# Revit family: XDiverter_Valve_Trim-American_Standard-Studio_S-T105.740
name_source: partatom
category: Plumbing Fixtures
revit_build: Autodesk Revit 2014 (Build: 20130308_1515(x64)
units: mm (PartAtom-declared; Revit-internal decimal feet)

## types (1)
- T105.740
    ADA Compliant = Yes
    Assembly Code = D2020300
    CW Connection = Yes
    CWFU = 3
    Connection Description = 1/2'' NPT Outlet Connection
    Default Elevation = 40"
    Description = Studio S Two-Handle Thermostat
    Distance From Wall = 2"
    Finish = Brass-American Standard-002-Polished Chrome
    HW Connection = Yes
    HWFU = 3
    Height = 3 13/16"
    Installation Type = Wall Mounted
    Length = 7 7/8"
    Manufacturer = American Standard
    Material = Brass-American Standard-002-Polished Chrome
    Model = T105.740
    Outlet Diameter Connection = 0"
    Price = Prices may vary. Please consult Manufacturer Representative for most up-to-date price list.
    Product Documentation Link = https://www.americanstandard-us.com
    Product Page URL = https://www.americanstandard-us.com
    R520 Rough Valve Body only = No
    R522 Rough Valve Body only = No
    R523 Rough Valve Body only = No
    R540 Rough Valve Body only = No
    Specification = Two-handle Thermostat shall feature a cast brass valve body. Thermostat shall be a wax element shuttle valve. Shall also feature ceramic disc valving, 1/2in NPT or 3/4in NPT inlets and outlets.
    URL = https://www.americanstandard-us.com
    Vent Connection = No
    WFU = 4
    Warranty Information = One Year Limited Warranty
    Waste Connection = Yes
    Water Connection Diameter = 1/2"
    Water Inlet Connection Description = 1/2'' NPT Inlet Supply Connection
    Water Outlet Connection Description = 1/2'' NPT Outlet Supply Connection
    Width = 7 7/8"

## geometry (parser evidence)
native form markers: Sweep x2
no freeform markers — native parametric forms only
